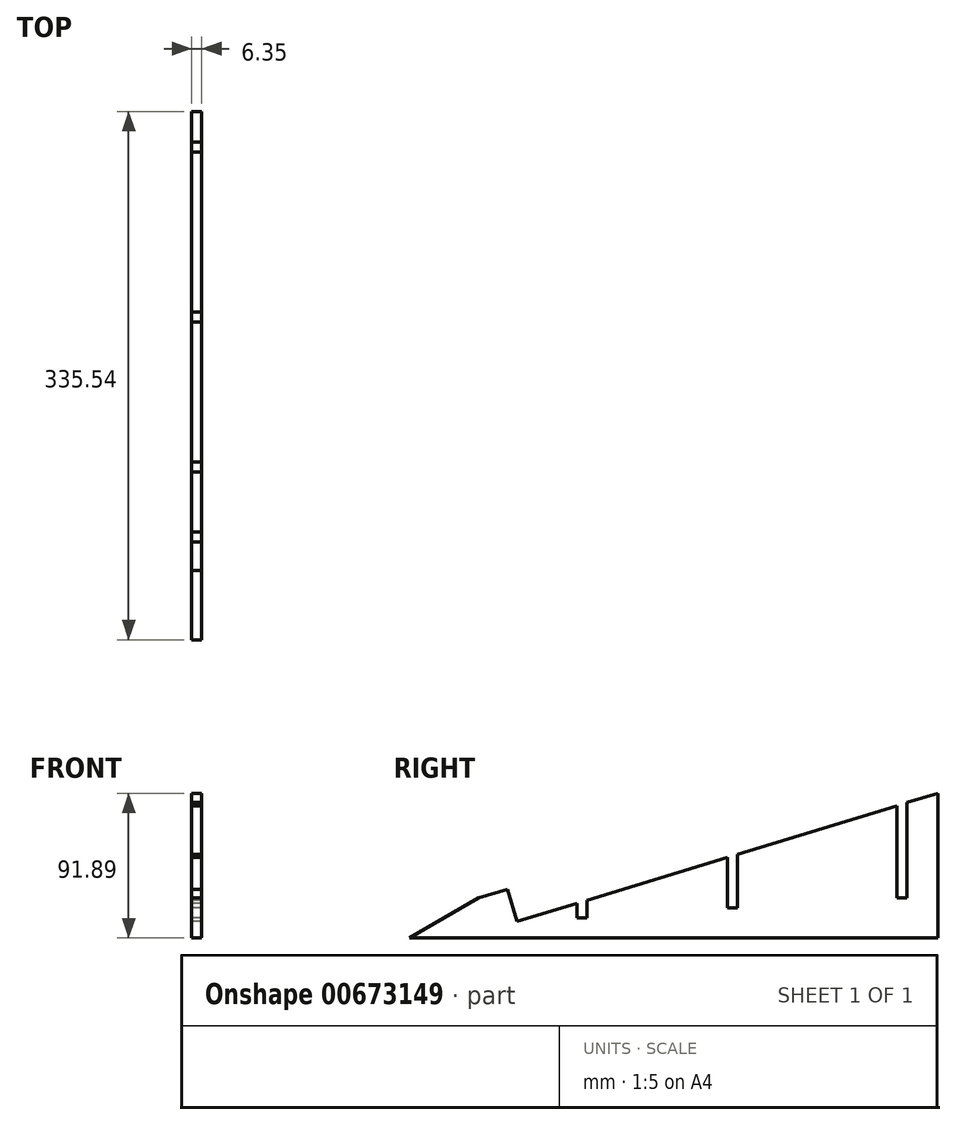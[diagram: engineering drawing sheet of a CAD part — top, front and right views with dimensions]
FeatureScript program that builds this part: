
annotation { "Feature Type Name" : "Feature", "Feature Type Description" : "" }
export const myFeature = defineFeature(function(context is Context, id is Id, definition is map)
    precondition{}
    {
        {
            var Q0;
            Q0=qCreatedBy(makeId("Right.planeOp"),FACE);
            var sketch = newSketch(context, id + "F0", { "sketchPlane" : qUnion([Q0])});
            skLineSegment(sketch, "E0.top", {"start": v(-291.55, -25.4) * mm, "end": v(0, -25.4) * mm});
            skLineSegment(sketch, "E0.left", {"start": v(-291.55, 0) * mm, "end": v(-291.55, -25.4) * mm});
            skLineSegment(sketch, "E1", {"start": v(-273.33, 5.56) * mm, "end": v(-267.07, -14.94) * mm});
            skLineSegment(sketch, "E2.trimOffspring", {"start": v(-273.33, 5.56) * mm, "end": v(-291.55, 0) * mm});
            skLineSegment(sketch, "E3", {"start": v(-267.07, -14.94) * mm, "end": v(-228.97, -3.33) * mm});
            skLineSegment(sketch, "E4", {"start": v(0, 66.5) * mm, "end": v(0, -25.4) * mm});
            skLineSegment(sketch, "E5", {"start": v(-291.55, 0) * mm, "end": v(-335.54, -25.4) * mm});
            skLineSegment(sketch, "E6", {"start": v(-335.54, -25.4) * mm, "end": v(-291.55, -25.4) * mm});
            skLineSegment(sketch, "E7", {"start": v(-19.42, 60.57) * mm, "end": v(-19.42, 0) * mm});
            skLineSegment(sketch, "E8", {"start": v(-19.42, 0) * mm, "end": v(-25.77, 0) * mm});
            skLineSegment(sketch, "E9", {"start": v(-25.77, 0) * mm, "end": v(-25.77, 58.64) * mm});
            skLineSegment(sketch, "E10", {"start": v(-228.97, -12.7) * mm, "end": v(-222.62, -12.7) * mm});
            skLineSegment(sketch, "E11", {"start": v(-222.62, -12.7) * mm, "end": v(-222.62, -1.39) * mm});
            skLineSegment(sketch, "E12", {"start": v(-133.54, 25.78) * mm, "end": v(-133.54, -6.35) * mm});
            skLineSegment(sketch, "E13", {"start": v(-133.54, -6.35) * mm, "end": v(-127.19, -6.35) * mm});
            skLineSegment(sketch, "E14", {"start": v(-127.19, -6.35) * mm, "end": v(-127.19, 27.71) * mm});
            skLineSegment(sketch, "E15", {"start": v(-228.97, -12.7) * mm, "end": v(-228.97, -3.33) * mm});
            skLineSegment(sketch, "E16.trimOffspring", {"start": v(-222.62, -1.39) * mm, "end": v(-133.54, 25.78) * mm});
            skLineSegment(sketch, "E17.trimOffspring", {"start": v(-127.19, 27.71) * mm, "end": v(-25.77, 58.64) * mm});
            skLineSegment(sketch, "E18.trimOffspring", {"start": v(-19.42, 60.57) * mm, "end": v(0, 66.5) * mm});
            skSolve(sketch);
        }
        {
            var Q0;
            Q0 = qSketchRegion(id + "F0", true);
            extrude(context, id + "F1", {"entities" : qUnion([Q0]), "depth" : 6.35 * mm, "offsetDistance" : 25.4 * mm});
        }
    });
